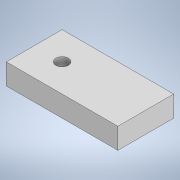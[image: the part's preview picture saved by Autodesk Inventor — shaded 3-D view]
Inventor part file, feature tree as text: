
AUTODESK INVENTOR PART (.ipt)
format: ipt  version: 2022 (Build 260153000, 153)  size: 96,256 bytes
history: native  units: mm
features: extrude x1, sketch x1
ambient origin geometry x8: Origin, YZ Plane, XZ Plane, XY Plane, X Axis, Y Axis, Z Axis, Center Point
bodies: Solid1 (feature_tree)
feature tree (2):
  extrude  "Extrusion1"  Depth=40.0mm
  sketch  "Sketch1"  dims[d0=80.0mm d1=40.0mm d2=20.0mm d3=20.0mm d4=9.0mm d5=15.0mm d6=0.0mm]
